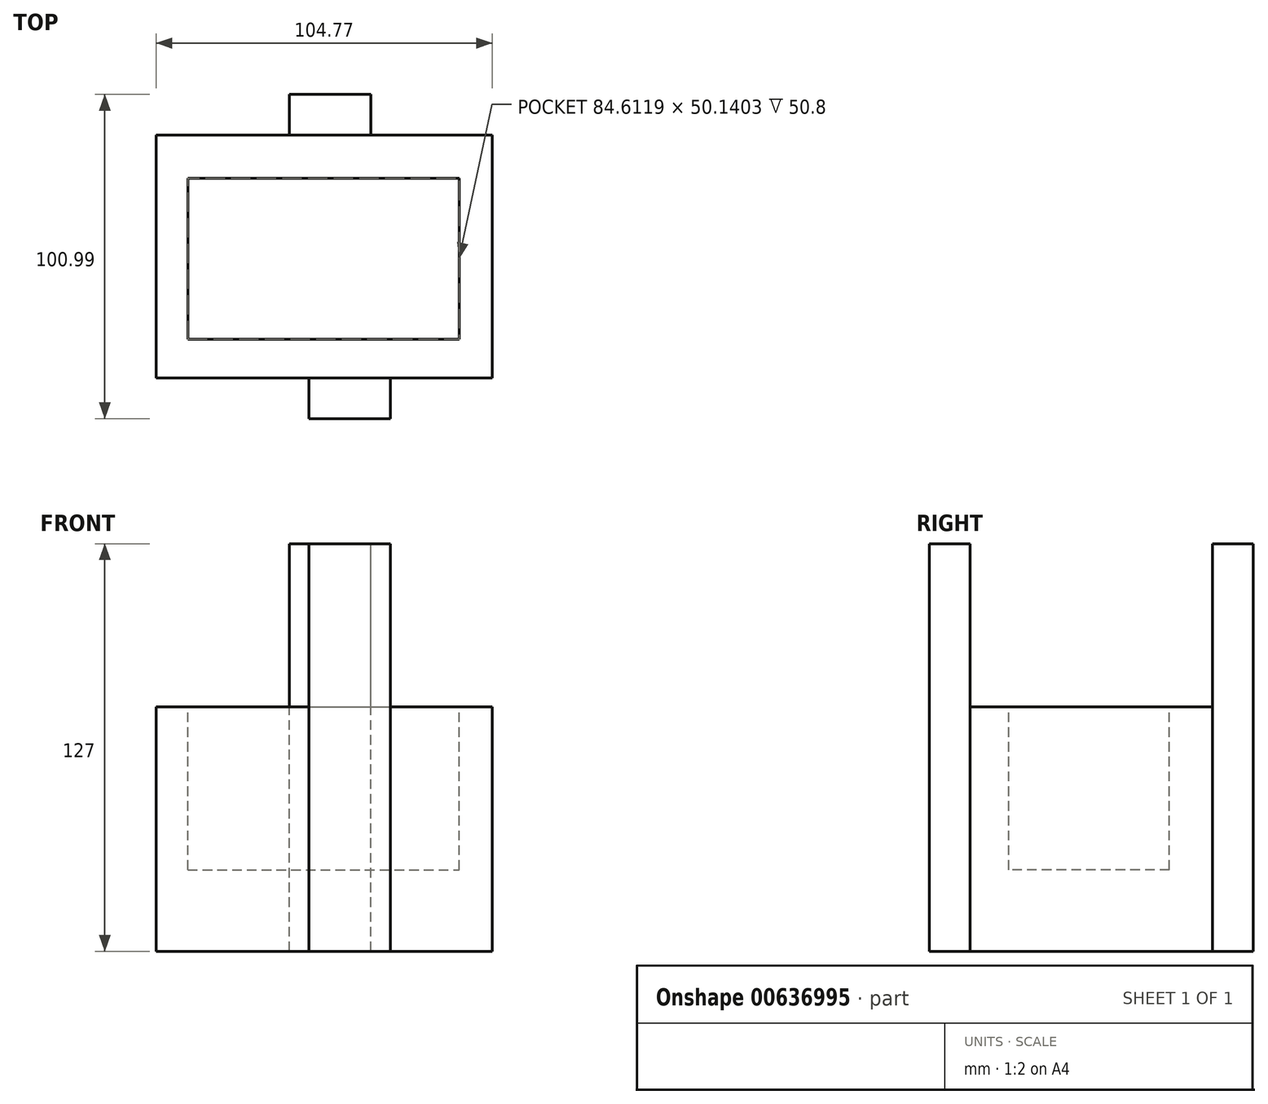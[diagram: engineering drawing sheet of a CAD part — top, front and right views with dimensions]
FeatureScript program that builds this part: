
annotation { "Feature Type Name" : "Feature", "Feature Type Description" : "" }
export const myFeature = defineFeature(function(context is Context, id is Id, definition is map)
    precondition{}
    {
        {
            var Q0;
            Q0=qCreatedBy(makeId("Top.planeOp"),FACE);
            var sketch = newSketch(context, id + "F0", { "sketchPlane" : qUnion([Q0])});
            skLineSegment(sketch, "E0.bottom", {"start": v(0, 0) * mm, "end": v(104.77, 0) * mm});
            skLineSegment(sketch, "E0.top", {"start": v(0, 75.59) * mm, "end": v(104.77, 75.59) * mm});
            skLineSegment(sketch, "E0.left", {"start": v(0, 0) * mm, "end": v(0, 75.59) * mm});
            skLineSegment(sketch, "E0.right", {"start": v(104.77, 0) * mm, "end": v(104.77, 75.59) * mm});
            skSolve(sketch);
        }
        {
            var Q0;
            Q0 = qSketchRegion(id + "F0", true);
            extrude(context, id + "F1", {"entities" : qUnion([Q0]), "depth" : 76.2 * mm, "offsetDistance" : 25.4 * mm});
        }
        {
            var Q0;
            Q0=makeQuery(id+"F1.opExtrude","CAP_FACE",FACE,{"disambiguationData":[OSD([sQuery(id+"F0.wireOp",EDGE,"E0.bottom"),sQuery(id+"F0.wireOp",EDGE,"E0.top"),sQuery(id+"F0.wireOp",EDGE,"E0.left"),sQuery(id+"F0.wireOp",EDGE,"E0.right")])],"isStart":false});
            var sketch = newSketch(context, id + "F2", { "sketchPlane" : qUnion([Q0])});
            skLineSegment(sketch, "E1.bottom", {"start": v(9.89, 62.2) * mm, "end": v(94.5, 62.2) * mm});
            skLineSegment(sketch, "E1.top", {"start": v(9.89, 12.06) * mm, "end": v(94.5, 12.06) * mm});
            skLineSegment(sketch, "E1.left", {"start": v(9.89, 62.2) * mm, "end": v(9.89, 12.06) * mm});
            skLineSegment(sketch, "E1.right", {"start": v(94.5, 62.2) * mm, "end": v(94.5, 12.06) * mm});
            skSolve(sketch);
        }
        {
            var Q0;
            Q0 = qSketchRegion(id + "F2", true);
            extrude(context, id + "F3", {"entities" : qUnion([Q0]), "operationType" : NewBodyOperationType.REMOVE, "oppositeDirection" : true, "depth" : 50.8 * mm, "offsetDistance" : 25.4 * mm});
        }
        {
            var Q0;
            Q0=makeQuery(id+"F1.opExtrude","SWEPT_FACE",FACE,{"disambiguationData":[OSD([sQuery(id+"F0.wireOp",EDGE,"E0.bottom")])]});
            var sketch = newSketch(context, id + "F4", { "sketchPlane" : qUnion([Q0])});
            skLineSegment(sketch, "E2.bottom", {"start": v(47.6, 0) * mm, "end": v(73, 0) * mm});
            skLineSegment(sketch, "E2.top", {"start": v(47.6, 127) * mm, "end": v(73, 127) * mm});
            skLineSegment(sketch, "E2.left", {"start": v(47.6, 0) * mm, "end": v(47.6, 127) * mm});
            skLineSegment(sketch, "E2.right", {"start": v(73, 0) * mm, "end": v(73, 127) * mm});
            skSolve(sketch);
        }
        {
            var Q0;
            Q0 = qSketchRegion(id + "F4", true);
            extrude(context, id + "F5", {"entities" : qUnion([Q0]), "operationType" : NewBodyOperationType.ADD, "depth" : 12.7 * mm, "offsetDistance" : 25.4 * mm});
        }
        {
            var Q0;
            Q0=makeQuery(id+"F1.opExtrude","SWEPT_FACE",FACE,{"disambiguationData":[OSD([sQuery(id+"F0.wireOp",EDGE,"E0.top")])]});
            var sketch = newSketch(context, id + "F6", { "sketchPlane" : qUnion([Q0])});
            skLineSegment(sketch, "E3.bottom", {"start": v(-66.95, 0) * mm, "end": v(-41.55, 0) * mm});
            skLineSegment(sketch, "E3.top", {"start": v(-66.95, 127) * mm, "end": v(-41.55, 127) * mm});
            skLineSegment(sketch, "E3.left", {"start": v(-66.95, 0) * mm, "end": v(-66.95, 127) * mm});
            skLineSegment(sketch, "E3.right", {"start": v(-41.55, 0) * mm, "end": v(-41.55, 127) * mm});
            skSolve(sketch);
        }
        {
            var Q0;
            Q0 = qSketchRegion(id + "F6", true);
            extrude(context, id + "F7", {"entities" : qUnion([Q0]), "operationType" : NewBodyOperationType.ADD, "depth" : 12.7 * mm, "offsetDistance" : 25.4 * mm});
        }
    });
